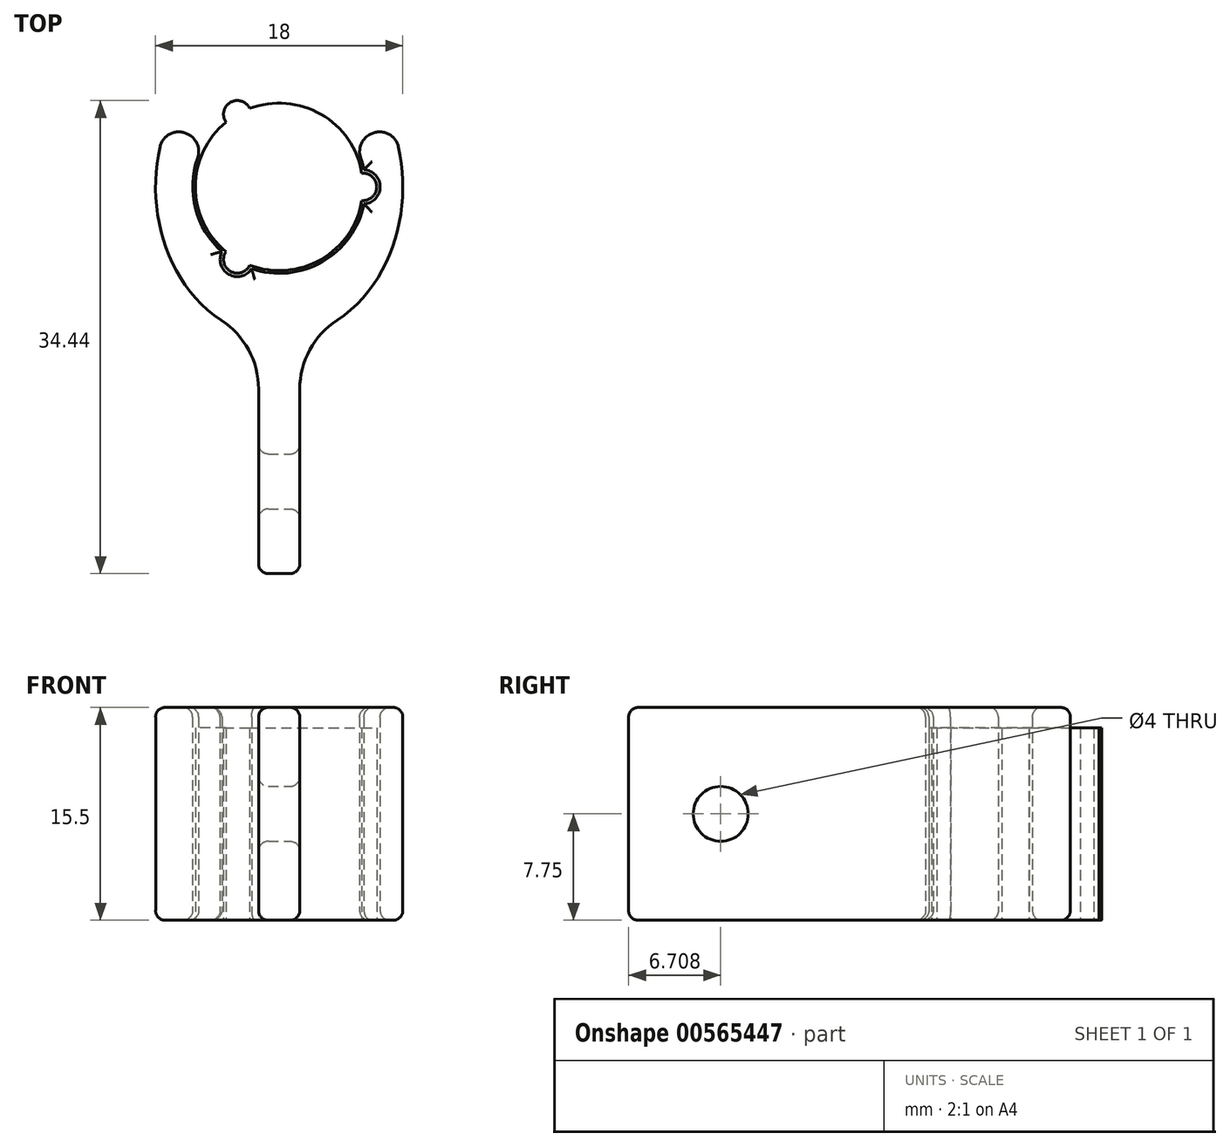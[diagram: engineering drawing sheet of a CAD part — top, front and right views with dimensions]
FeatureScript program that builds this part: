
annotation { "Feature Type Name" : "Feature", "Feature Type Description" : "" }
export const myFeature = defineFeature(function(context is Context, id is Id, definition is map)
    precondition{}
    {
        {
            var Q0;
            Q0=qCreatedBy(makeId("Top.planeOp"),FACE);
            var sketch = newSketch(context, id + "F0", { "sketchPlane" : qUnion([Q0])});
            skArc(sketch, "E0", {"start": v(-3.87, 4.71) * mm, "mid": v(-6.1, 0) * mm, "end": v(-3.87, -4.71) * mm});
            skArc(sketch, "E1", {"start": v(6.02, -1) * mm, "mid": v(7.1, 0) * mm, "end": v(6.02, 1) * mm});
            skArc(sketch, "E2.1.0", {"start": v(-2.15, 5.71) * mm, "mid": v(-3.55, 6.15) * mm, "end": v(-3.87, 4.71) * mm});
            skArc(sketch, "E2.2.0", {"start": v(-3.87, -4.71) * mm, "mid": v(-3.55, -6.15) * mm, "end": v(-2.15, -5.71) * mm});
            skArc(sketch, "E3.trimOffspring", {"start": v(-2.15, -5.71) * mm, "mid": v(3.05, -5.28) * mm, "end": v(6.02, -1) * mm});
            skArc(sketch, "E4.trimOffspring", {"start": v(6.02, 1) * mm, "mid": v(3.05, 5.28) * mm, "end": v(-2.15, 5.71) * mm});
            skSolve(sketch);
        }
        {
            var Q0;
            Q0 = qSketchRegion(id + "F0", true);
            extrude(context, id + "F1", {"entities" : qUnion([Q0]), "depth" : 14 * mm, "offsetDistance" : 25 * mm});
        }
        {
            var Q0;
            Q0=qCreatedBy(makeId("Top.planeOp"),FACE);
            var sketch = newSketch(context, id + "F2", { "sketchPlane" : qUnion([Q0]), "disableImprinting" : false});
            skArc(sketch, "E5", {"start": v(-7.19, 4.15) * mm, "mid": v(-8, -2.2) * mm, "end": v(-4.06, -7.24) * mm, "construction": true});
            skArc(sketch, "E6", {"start": v(-2, -5.97) * mm, "mid": v(3.15, -5.46) * mm, "end": v(6.18, -1.25) * mm});
            skArc(sketch, "E7", {"start": v(6.18, -1.25) * mm, "mid": v(7.35, 0) * mm, "end": v(6.18, 1.25) * mm});
            skLineSegment(sketch, "E8", {"start": v(-6.3, 0) * mm, "end": v(-6.3, 9.56) * mm, "construction": true});
            skLineSegment(sketch, "E9", {"start": v(-5.8, 2.46) * mm, "end": v(-5.8, 0) * mm});
            skLineSegment(sketch, "E10", {"start": v(-5.8, 0) * mm, "end": v(-5.67, 0.15) * mm, "construction": true});
            skArc(sketch, "E11", {"start": v(-4.17, -4.72) * mm, "mid": v(-3.68, -6.37) * mm, "end": v(-2, -5.97) * mm});
            skArc(sketch, "E12.trimOffspring", {"start": v(-5.94, 2.1) * mm, "mid": v(-6.1, -1.58) * mm, "end": v(-4.17, -4.72) * mm});
            skLineSegment(sketch, "E13", {"start": v(17.36, -6.4) * mm, "end": v(17.36, -1.07) * mm});
            skLineSegment(sketch, "E14", {"start": v(18.36, -0.07) * mm, "end": v(20.06, -0.07) * mm});
            skPoint(sketch, "E15.visualSharp", {"position": v(17.36, -0.07) * mm});
            skArc(sketch, "E15.filletArc", {"start": v(18.36, -0.07) * mm, "mid": v(17.66, -0.36) * mm, "end": v(17.36, -1.07) * mm});
            skPoint(sketch, "E16.orphan", {"position": v(-5.8, 9.56) * mm});
            skPoint(sketch, "E17.visualSharp", {"position": v(-5.8, 5.94) * mm});
            skPoint(sketch, "E18.visualSharp", {"position": v(6.18, 5.55) * mm});
            skLineSegment(sketch, "E19.bottom", {"start": v(1.5, -28.16) * mm, "end": v(-1.5, -28.16) * mm});
            skLineSegment(sketch, "E19.left", {"start": v(1.5, -28.16) * mm, "end": v(1.5, -14.74) * mm});
            skLineSegment(sketch, "E19.right", {"start": v(-1.5, -28.16) * mm, "end": v(-1.5, -14.74) * mm});
            skPoint(sketch, "E19.middle", {"position": v(0, -17.88) * mm});
            skLineSegment(sketch, "E20", {"start": v(0, 0) * mm, "end": v(0, -16.8) * mm, "construction": true});
            skPoint(sketch, "E21.orphan", {"position": v(-1.5, -7.6) * mm});
            skArc(sketch, "E22.trimOffspring", {"start": v(4.06, -7.24) * mm, "mid": v(8, -2.2) * mm, "end": v(7.19, 4.15) * mm, "construction": true});
            skPoint(sketch, "E23.orphan", {"position": v(1.5, -7.6) * mm});
            skPoint(sketch, "E24.visualSharp", {"position": v(1.5, -8.16) * mm});
            skArc(sketch, "E24.filletArc", {"start": v(4.06, -7.24) * mm, "mid": v(2.19, -9.08) * mm, "end": v(1.5, -11.6) * mm, "construction": true});
            skPoint(sketch, "E25.visualSharp", {"position": v(-1.5, -8.16) * mm});
            skArc(sketch, "E25.filletArc", {"start": v(-1.5, -11.6) * mm, "mid": v(-2.19, -9.08) * mm, "end": v(-4.06, -7.24) * mm, "construction": true});
            skEllipticalArc(sketch, "E26", {});
            skLineSegment(sketch, "E27", {"start": v(-6.56, 3.79) * mm, "end": v(-6.61, 3.82) * mm});
            skLineSegment(sketch, "E28.MirrorCS", {"start": v(6.56, 3.79) * mm, "end": v(6.61, 3.82) * mm});
            skPoint(sketch, "E29.0.visualSharp", {"position": v(-8.14, 4.7) * mm});
            skArc(sketch, "E29.0.filletArc", {"start": v(-6.61, 3.82) * mm, "mid": v(-7.87, 3.89) * mm, "end": v(-8.68, 2.91) * mm});
            skPoint(sketch, "E29.1.visualSharp", {"position": v(-5.46, 3.15) * mm});
            skArc(sketch, "E29.1.filletArc", {"start": v(-5.94, 2.1) * mm, "mid": v(-5.94, 3.06) * mm, "end": v(-6.56, 3.79) * mm});
            skPoint(sketch, "E29.2.visualSharp", {"position": v(5.46, 3.15) * mm});
            skArc(sketch, "E29.2.filletArc", {"start": v(6.56, 3.79) * mm, "mid": v(5.94, 3.06) * mm, "end": v(5.94, 2.1) * mm});
            skPoint(sketch, "E29.3.visualSharp", {"position": v(8.14, 4.7) * mm});
            skArc(sketch, "E29.3.filletArc", {"start": v(8.68, 2.91) * mm, "mid": v(7.87, 3.89) * mm, "end": v(6.61, 3.82) * mm});
            skEllipticalArc(sketch, "E30.trimOffspring", {});
            skPoint(sketch, "E31.0.visualSharp", {"position": v(-1.5, -10.85) * mm});
            skArc(sketch, "E31.0.filletArc", {"start": v(-1.5, -14.74) * mm, "mid": v(-2.23, -11.88) * mm, "end": v(-4.23, -9.71) * mm});
            skPoint(sketch, "E31.1.visualSharp", {"position": v(1.5, -10.85) * mm});
            skArc(sketch, "E31.1.filletArc", {"start": v(4.23, -9.71) * mm, "mid": v(2.23, -11.88) * mm, "end": v(1.5, -14.74) * mm});
            skArc(sketch, "E32.trimOffspring", {"start": v(6.18, 1.25) * mm, "mid": v(6.07, 1.68) * mm, "end": v(5.94, 2.1) * mm});
            const initialGuessF2  = {"E26": [0, 0, 0, -1, 0.011, 0.009, 4.4444345907775, 5.794100531796251], "E30.trimOffspring": [0, 0, 0, -1, 0.011, 0.009, 0.489084775383335, 1.8387507164020866]};
            skSetInitialGuess(sketch, initialGuessF2);
            skSolve(sketch);
        }
        {
            var Q0;
            Q0 = qSketchRegion(id + "F2", true);
            extrude(context, id + "F3", {"entities" : qUnion([Q0]), "flatOperationType" : FlatOperationType.REMOVE, "thickness1" : 5 * mm, "thickness2" : 0 * mm, "thickness" : 5 * mm, "depth" : 15.5 * mm, "offsetDistance" : 25 * mm, "startOffsetBound" : StartOffsetType.BLIND, "startOffsetDistance" : 25 * mm, "domain" : OperationDomain.MODEL});
        }
        {
            var Q0;
            Q0=makeQuery(id+"F3.opExtrude","SWEPT_FACE",FACE,{"disambiguationData":[OSD([sQuery(id+"F2.wireOp",EDGE,"E19.left")])]});
            var sketch = newSketch(context, id + "F4", { "sketchPlane" : qUnion([Q0]), "disableImprinting" : false});
            skCircle(sketch, "E33", {"center": v(-21.45, 7.75) * mm, "radius": 2 * mm});
            skLineSegment(sketch, "E34", {"start": v(-21.45, 15.5) * mm, "end": v(-21.45, 0) * mm, "construction": true});
            skLineSegment(sketch, "E35", {"start": v(-28.16, 7.75) * mm, "end": v(-43.72, 7.75) * mm, "construction": true});
            skSolve(sketch);
        }
        {
            var Q0;
            Q0 = qSketchRegion(id + "F4", true);
            extrude(context, id + "F5", {"entities" : qUnion([Q0]), "operationType" : NewBodyOperationType.REMOVE, "endBound" : BoundingType.THROUGH_ALL, "oppositeDirection" : true, "depth" : 25 * mm, "offsetDistance" : 25 * mm});
        }
        {
            var Q0;
            Q0=makeQuery(id+"F3.opExtrude","CAP_FACE",FACE,{"disambiguationData":[OSD([sQuery(id+"F2.wireOp",EDGE,"E5"),sQuery(id+"F2.wireOp",EDGE,"E6"),sQuery(id+"F2.wireOp",EDGE,"E7"),sQuery(id+"F2.wireOp",EDGE,"EAZYVOWo-AO1C-EaVK-qxZe-mT13O62GOpMt"),sQuery(id+"F2.wireOp",EDGE,"E9"),sQuery(id+"F2.wireOp",EDGE,"E11"),sQuery(id+"F2.wireOp",EDGE,"E12.trimOffspring"),sQuery(id+"F2.wireOp",EDGE,"E17.filletArc"),sQuery(id+"F2.wireOp",EDGE,"E18.filletArc"),sQuery(id+"F2.wireOp",EDGE,"E19.bottom"),sQuery(id+"F2.wireOp",EDGE,"E19.left"),sQuery(id+"F2.wireOp",EDGE,"E19.right"),sQuery(id+"F2.wireOp",EDGE,"E22.trimOffspring"),sQuery(id+"F2.wireOp",EDGE,"E24.filletArc"),sQuery(id+"F2.wireOp",EDGE,"E25.filletArc")])],"isStart":false});
            var Q1;
            Q1=makeQuery(id+"F3.opExtrude","SWEPT_FACE",FACE,{"disambiguationData":[OSD([sQuery(id+"F2.wireOp",EDGE,"E19.bottom")])]});
            var Q2;
            Q2=makeQuery(id+"F3.opExtrude","CAP_FACE",FACE,{"disambiguationData":[OSD([sQuery(id+"F2.wireOp",EDGE,"E5"),sQuery(id+"F2.wireOp",EDGE,"E6"),sQuery(id+"F2.wireOp",EDGE,"E7"),sQuery(id+"F2.wireOp",EDGE,"EAZYVOWo-AO1C-EaVK-qxZe-mT13O62GOpMt"),sQuery(id+"F2.wireOp",EDGE,"E9"),sQuery(id+"F2.wireOp",EDGE,"E11"),sQuery(id+"F2.wireOp",EDGE,"E12.trimOffspring"),sQuery(id+"F2.wireOp",EDGE,"E17.filletArc"),sQuery(id+"F2.wireOp",EDGE,"E18.filletArc"),sQuery(id+"F2.wireOp",EDGE,"E19.bottom"),sQuery(id+"F2.wireOp",EDGE,"E19.left"),sQuery(id+"F2.wireOp",EDGE,"E19.right"),sQuery(id+"F2.wireOp",EDGE,"E22.trimOffspring"),sQuery(id+"F2.wireOp",EDGE,"E24.filletArc"),sQuery(id+"F2.wireOp",EDGE,"E25.filletArc")])],"isStart":true});
            var Q3;
            Q3=makeQuery(id+"F5.boolean.opBoolean","COPY",FACE,{"derivedFrom":makeQuery(id+"F5.opExtrude","SWEPT_FACE",FACE,{"disambiguationData":[OSD([sQuery(id+"F4.wireOp",EDGE,"E33")])]})});
            fillet(context, id + "F6", {"entities" : qUnion([Q0, Q1, Q2, Q3]), "radius" : 0.7 * mm, "width" : 5 * mm, "tangentPropagation" : true, "blendControlType" : BlendControlType.RADIUS, "defaultsChanged" : true, "isAsymmetric" : false, "otherRadius" : 5 * mm, "flipAsymmetric" : false, "isPartial" : false, "partialFirstEdgeTotalParameter" : 0.01, "partialOppositeParameter" : true, "secondBound" : false, "partialSecondEdgeTotalParameter" : 0.99, "vertexSettings" : [], "pointOnEdgeSettings" : [], "allowEdgeOverflow" : false, "smoothCorners" : false, "filletType" : FilletType.EDGE});
        }
    });
